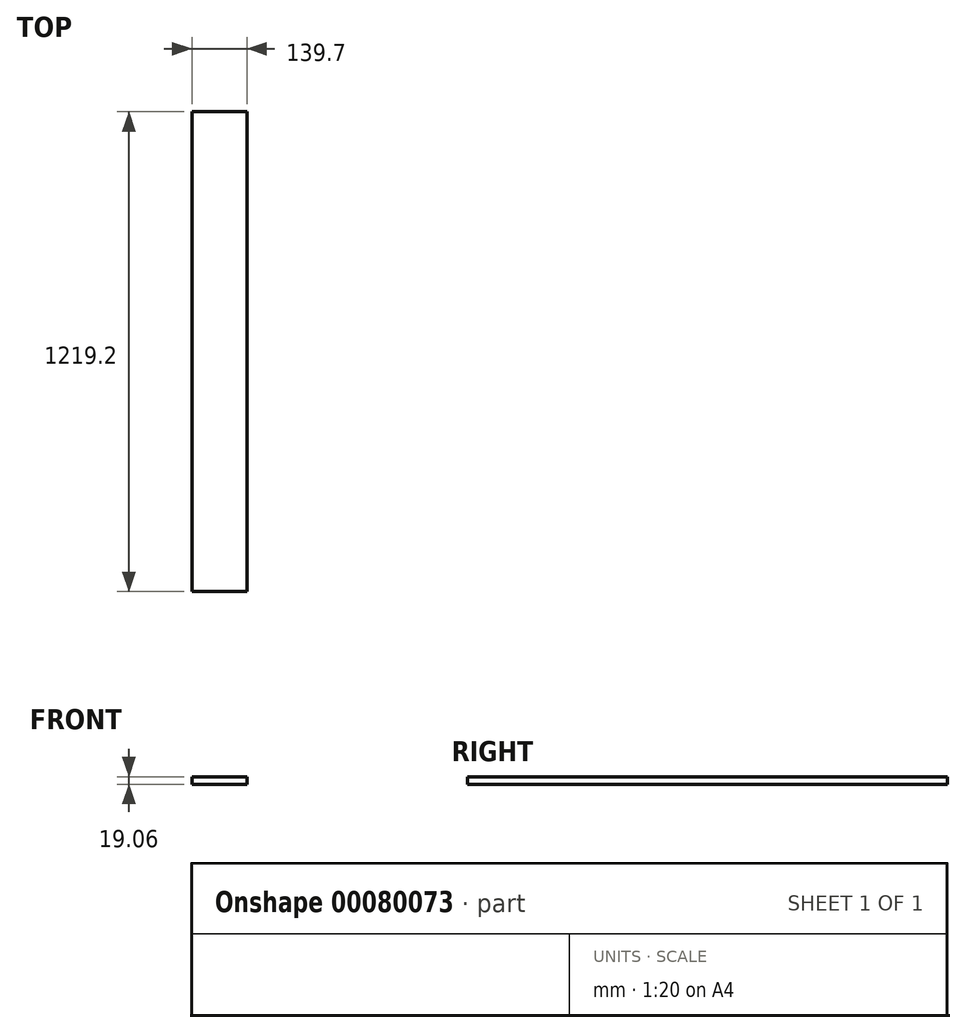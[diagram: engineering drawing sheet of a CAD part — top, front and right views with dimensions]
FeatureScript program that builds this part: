
annotation { "Feature Type Name" : "Feature", "Feature Type Description" : "" }
export const myFeature = defineFeature(function(context is Context, id is Id, definition is map)
    precondition{}
    {
        {
            var Q0;
            Q0=qCreatedBy(makeId("Front.planeOp"),FACE);
            var sketch = newSketch(context, id + "F0", { "sketchPlane" : qUnion([Q0])});
            skLineSegment(sketch, "E0.bottom", {"start": v(-69.85, 9.53) * mm, "end": v(69.85, 9.53) * mm});
            skLineSegment(sketch, "E0.top", {"start": v(-69.85, -9.52) * mm, "end": v(69.85, -9.52) * mm});
            skLineSegment(sketch, "E0.left", {"start": v(-69.85, 9.53) * mm, "end": v(-69.85, -9.52) * mm});
            skLineSegment(sketch, "E0.right", {"start": v(69.85, 9.53) * mm, "end": v(69.85, -9.52) * mm});
            skPoint(sketch, "E0.middle", {"position": v(0, 0) * mm});
            skSolve(sketch);
        }
        {
            var Q0;
            Q0 = qSketchRegion(id + "F0", true);
            extrude(context, id + "F1", {"entities" : qUnion([Q0]), "endBound" : BoundingType.SYMMETRIC, "depth" : 1219.2 * mm});
        }
    });
